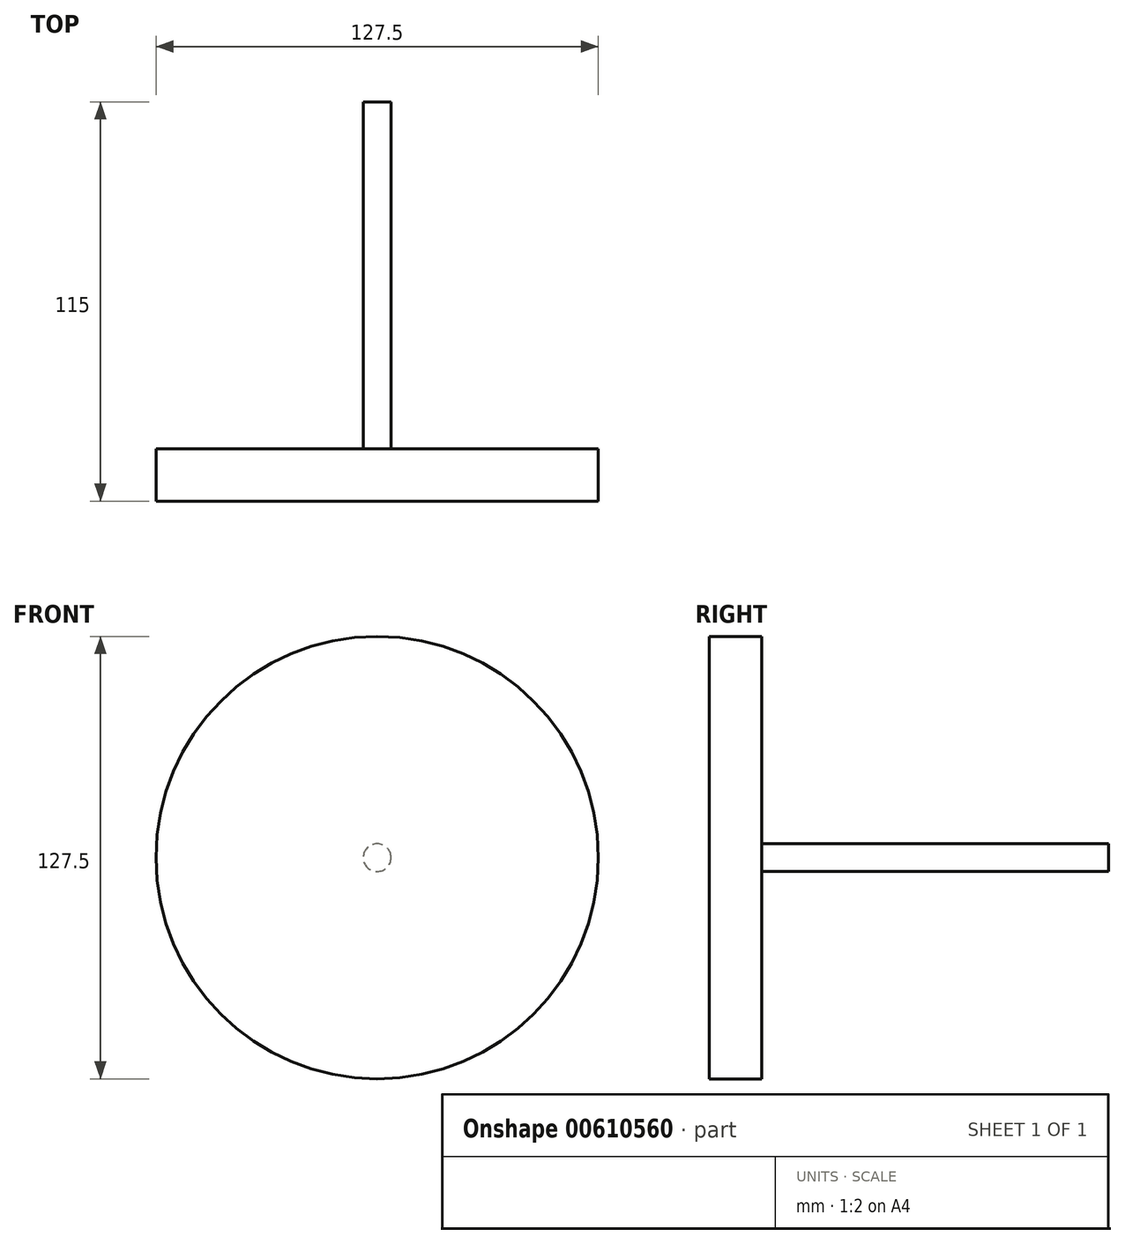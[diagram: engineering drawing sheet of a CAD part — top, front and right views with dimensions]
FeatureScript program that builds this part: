
annotation { "Feature Type Name" : "Feature", "Feature Type Description" : "" }
export const myFeature = defineFeature(function(context is Context, id is Id, definition is map)
    precondition{}
    {
        {
            var Q0;
            Q0=qCreatedBy(makeId("Front.planeOp"),FACE);
            var sketch = newSketch(context, id + "F0", { "sketchPlane" : qUnion([Q0])});
            skCircle(sketch, "E0", {"center": v(0, 0) * mm, "radius": 63.75 * mm});
            skCircle(sketch, "E1", {"center": v(0, 0) * mm, "radius": 70 * mm, "construction": true});
            skCircle(sketch, "E2", {"center": v(0, 0) * mm, "radius": 75 * mm, "construction": true});
            skLineSegment(sketch, "E3", {"start": v(0, 0) * mm, "end": v(0, 142.53) * mm, "construction": true});
            skLineSegment(sketch, "E4", {"start": v(0, 0) * mm, "end": v(-8.3, 147.71) * mm, "construction": true});
            skLineSegment(sketch, "E5", {"start": v(0, 70) * mm, "end": v(-109.9, 70) * mm, "construction": true});
            skLineSegment(sketch, "E6", {"start": v(0, 70) * mm, "end": v(-107.13, 31) * mm, "construction": true});
            skCircle(sketch, "E7", {"center": v(0, 0) * mm, "radius": 65.78 * mm, "construction": true});
            skCircle(sketch, "E8", {"center": v(0, 70) * mm, "radius": 17.5 * mm, "construction": true});
            skCircle(sketch, "E9", {"center": v(-16.33, 63.72) * mm, "radius": 17.5 * mm, "construction": true});
            skArc(sketch, "E10", {"start": v(-2.9, 74.94) * mm, "mid": v(0.11, 69.7) * mm, "end": v(1.17, 63.74) * mm});
            skArc(sketch, "E11.MirrorCS", {"start": v(-5.5, 74.8) * mm, "mid": v(-7.91, 69.25) * mm, "end": v(-8.3, 63.2) * mm});
            skArc(sketch, "E12", {"start": v(-5.5, 74.8) * mm, "mid": v(-4.2, 74.88) * mm, "end": v(-2.9, 74.94) * mm});
            skCircle(sketch, "E13", {"center": v(0, 0) * mm, "radius": 25 * mm});
            skSolve(sketch);
        }
        {
            var Q0;
            {var subQ0=sQuery(id+"F0.wireOp",EDGE,"E0");var subQ1=makeQuery(id+"F0.imprint","INTERSECT",VERTEX,{"derivedFrom":[subQ0,sQuery(id+"F0.wireOp",EDGE,"E10")]});Q0=makeQuery(id+"F0.imprint","IMPRINT",FACE,{"disambiguationData":[TD([[makeQuery(id+"F0.imprint","IMPRINT",EDGE,{"disambiguationData":[TD([[subQ1,-1.0]])],"derivedFrom":subQ0}),1.0]])]});}
            var Q1;
            {var subQ0=sQuery(id+"F0.wireOp",EDGE,"E10");Q1=makeQuery(id+"F0.imprint","IMPRINT",FACE,{"disambiguationData":[TD([[makeQuery(id+"F0.imprint","IMPRINT",EDGE,{"derivedFrom":subQ0}),-1.0]])]});}
            var Q2;
            Q2=makeQuery(id+"F0.imprint","IMPRINT",FACE,{"disambiguationData":[TD([[makeQuery(id+"F0.imprint","IMPRINT",EDGE,{"derivedFrom":sQuery(id+"F0.wireOp",EDGE,"E13")}),1.0]])]});
            extrude(context, id + "F1", {"entities" : qUnion([Q0, Q1, Q2]), "depth" : 15 * mm, "offsetDistance" : 25.4 * mm});
        }
        {
            var Q0;
            Q0=makeQuery(id+"F1.opExtrude","SWEPT_BODY",BODY,{"disambiguationData":[OSD([sQuery(id+"F0.wireOp",EDGE,"E0"),sQuery(id+"F0.wireOp",EDGE,"E10"),sQuery(id+"F0.wireOp",EDGE,"E11.MirrorCS"),sQuery(id+"F0.wireOp",EDGE,"E12")])]});
            var Q1;
            Q1=makeQuery(id+"F1.opExtrude","SWEPT_FACE",FACE,{"disambiguationData":[OSD([sQuery(id+"F0.wireOp",EDGE,"E0")])]});
            circularPattern(context, id + "F2", {"entities" : qUnion([Q0]), "axis" : qUnion([Q1]), "angle" : 360 * degree, "instanceCount" : 28, "equalSpace" : true});
        }
        {
            var Q0;
            Q0=makeQuery(id+"F2.opPattern","COPY",BODY,{"derivedFrom":makeQuery(id+"F1.opExtrude","SWEPT_BODY",BODY,{"disambiguationData":[OSD([sQuery(id+"F0.wireOp",EDGE,"E0"),sQuery(id+"F0.wireOp",EDGE,"E10"),sQuery(id+"F0.wireOp",EDGE,"E11.MirrorCS"),sQuery(id+"F0.wireOp",EDGE,"E12")])]}),"instanceName":"9"});
            var Q1;
            Q1=sQuery(id+"F0.wireOp",VERTEX,"E7.center");
            transform(context, id + "F3", {"entities" : qUnion([Q0]), "transformType" : TransformType.SCALE_UNIFORMLY, "scale" : 0.3, "scalePoint" : qUnion([Q1]), "makeCopy" : false});
        }
        {
            var Q0;
            Q0=makeQuery(id+"F0.imprint","IMPRINT",FACE,{"disambiguationData":[TD([[makeQuery(id+"F0.imprint","IMPRINT",EDGE,{"derivedFrom":sQuery(id+"F0.wireOp",EDGE,"E13")}),1.0]])]});
            var sketch = newSketch(context, id + "F4", { "sketchPlane" : qUnion([Q0])});
            skCircle(sketch, "E14", {"center": v(0, 0) * mm, "radius": 4 * mm});
            skSolve(sketch);
        }
        {
            var Q0;
            Q0=makeQuery(id+"F4.imprint","IMPRINT",FACE,{"disambiguationData":[TD([[makeQuery(id+"F4.imprint","IMPRINT",EDGE,{"derivedFrom":sQuery(id+"F4.wireOp",EDGE,"E14")}),1.0]])]});
            var Q1;
            Q1=sQuery(id+"F4.wireOp",EDGE,"E14");
            extrude(context, id + "F5", {"entities" : qUnion([Q0]), "operationType" : NewBodyOperationType.ADD, "surfaceEntities" : qUnion([Q1]), "oppositeDirection" : true, "depth" : 100 * mm, "offsetDistance" : 25.4 * mm});
        }
    });
